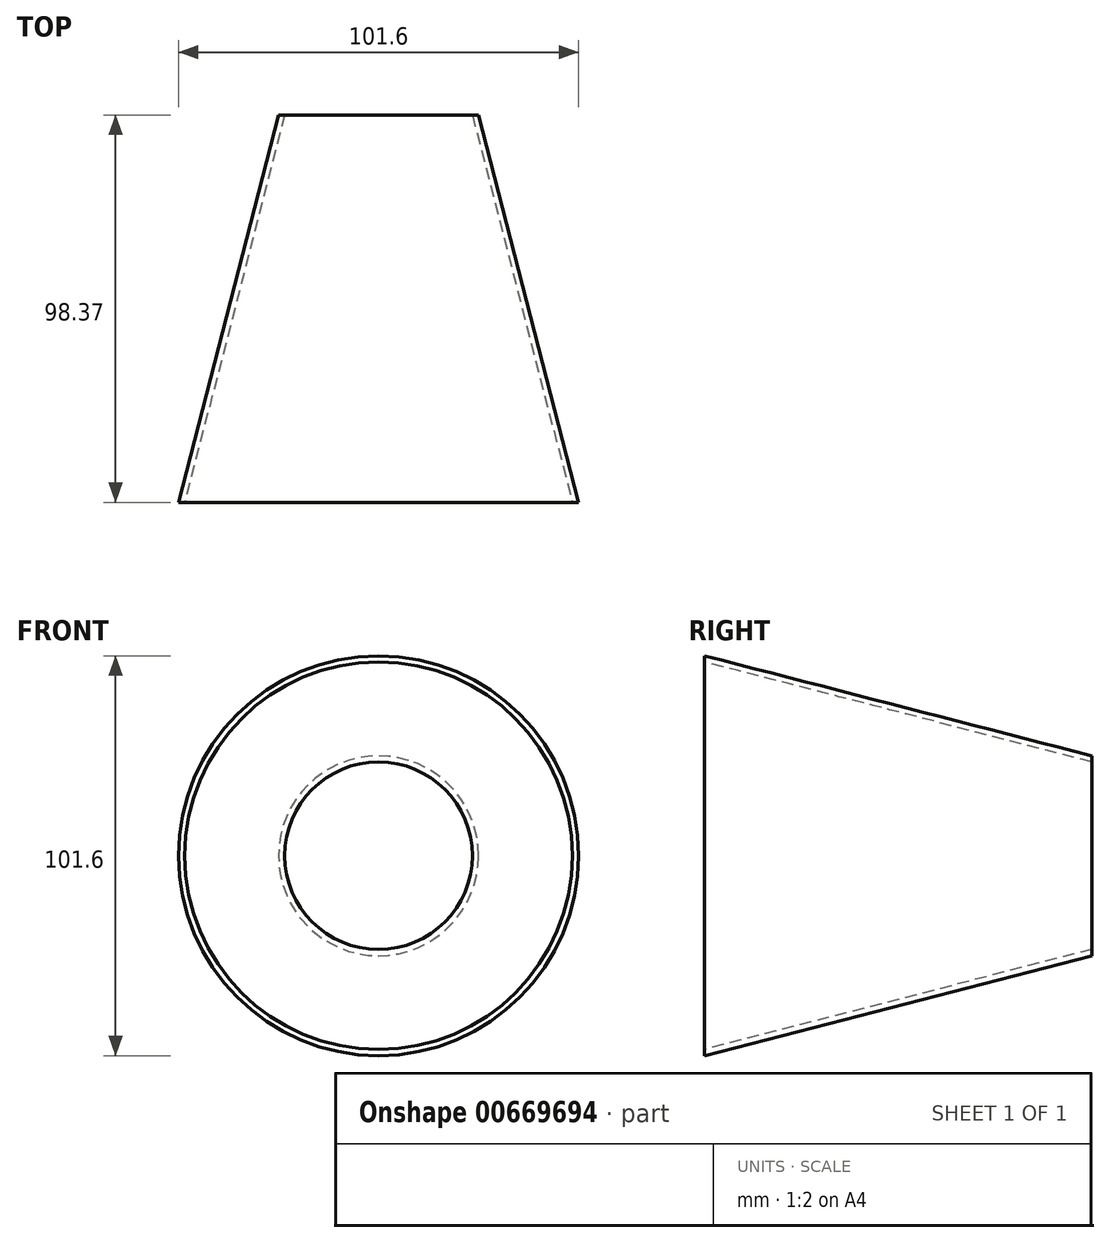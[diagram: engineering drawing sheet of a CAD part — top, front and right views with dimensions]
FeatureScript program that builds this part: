
annotation { "Feature Type Name" : "Feature", "Feature Type Description" : "" }
export const myFeature = defineFeature(function(context is Context, id is Id, definition is map)
    precondition{}
    {
        {
            var Q0;
            Q0=qCreatedBy(makeId("Front.planeOp"),FACE);
            var sketch = newSketch(context, id + "F0", { "sketchPlane" : qUnion([Q0])});
            skCircle(sketch, "E0", {"center": v(0, 0) * mm, "radius": 50.8 * mm});
            skCircle(sketch, "E1.0", {"center": v(0, 0) * mm, "radius": 49.28 * mm});
            skSolve(sketch);
        }
        {
            var Q0;
            Q0=qCreatedBy(makeId("Right.planeOp"),FACE);
            var sketch = newSketch(context, id + "F1", { "sketchPlane" : qUnion([Q0])});
            skLineSegment(sketch, "E2.0", {"start": v(0, -49.28) * mm, "end": v(0, -49.23) * mm});
            skLineSegment(sketch, "E3", {"start": v(-15.79, 0) * mm, "end": v(90.51, 0) * mm, "construction": true});
            skLineSegment(sketch, "E4", {"start": v(90.51, 0) * mm, "end": v(116.85, 0) * mm, "construction": true});
            skLineSegment(sketch, "E5", {"start": v(0, 50.8) * mm, "end": v(98.37, 25.4) * mm});
            skLineSegment(sketch, "E6", {"start": v(98.37, 25.4) * mm, "end": v(98.37, 0) * mm});
            skLineSegment(sketch, "E7.0", {"start": v(0, 49.23) * mm, "end": v(98.37, 23.83) * mm});
            skLineSegment(sketch, "E8.MirrorCS", {"start": v(0, -50.8) * mm, "end": v(98.37, -25.4) * mm});
            skLineSegment(sketch, "E9.MirrorCS", {"start": v(0, -49.23) * mm, "end": v(98.37, -23.83) * mm});
            skLineSegment(sketch, "E10.MirrorCS", {"start": v(98.37, -25.4) * mm, "end": v(98.37, 0) * mm});
            skLineSegment(sketch, "E11.trimOffspring", {"start": v(0, 49.23) * mm, "end": v(0, 50.8) * mm});
            skSolve(sketch);
        }
        {
            var Q0;
            {var subQ0=sQuery(id+"F1.wireOp",EDGE,"E5");Q0=makeQuery(id+"F1.imprint","IMPRINT",FACE,{"disambiguationData":[TD([[makeQuery(id+"F1.imprint","IMPRINT",EDGE,{"derivedFrom":subQ0}),-1.0]])]});}
            var Q1;
            Q1=sQuery(id+"F0.wireOp",EDGE,"E0");
            revolve(context, id + "F2", {"entities" : qUnion([Q0]), "axis" : qUnion([Q1]), "revolveType" : RevolveType.FULL});
        }
    });
